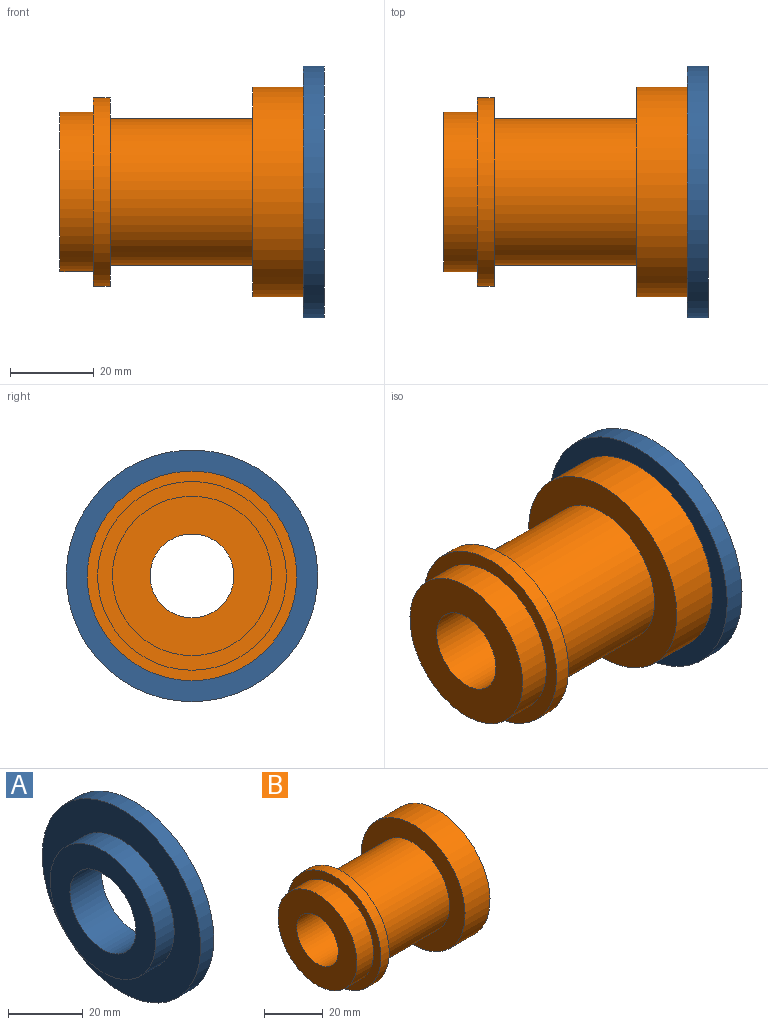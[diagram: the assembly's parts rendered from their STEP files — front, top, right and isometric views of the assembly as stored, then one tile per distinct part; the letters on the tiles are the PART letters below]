
ASSEMBLY  parts=2 mates=1
PART A: 6 faces, bbox 12x60x60 mm
  f0: cylinder r=12.5mm len=25mm, axis (1,0,0), area 942.5mm2, adj f1,f5
  f1: plane 60x60mm, normal (1,0,0), area 2336.6mm2, adj f0,f2
  f2: cylinder r=30mm len=60mm, axis (1,0,0), area 942.5mm2, adj f1,f3
  f3: plane 60x60mm, normal (-1,0,0), area 1570.8mm2, adj f2,f4
  f4: cylinder r=20mm len=40mm, axis (1,0,0), area 879.6mm2, adj f3,f5
  f5: plane 40x40mm, normal (-1,0,0), area 765.8mm2, adj f0,f4
PART B: 12 faces, bbox 58x50x50 mm
  f0: plane 50x50mm, normal (1,0,0), area 706.9mm2, adj f1,f11
  f1: cylinder r=25mm len=50mm, axis (1,0,0), area 1885mm2, adj f0,f2
  f2: plane 50x50mm, normal (-1,0,0), area 1001.4mm2, adj f1,f3
  f3: cylinder r=17.5mm len=35mm, axis (1,0,0), area 3738.5mm2, adj f2,f4
  f4: plane 45x45mm, normal (1,0,0), area 628.3mm2, adj f3,f5
  f5: cylinder r=22.5mm len=45mm, axis (1,0,0), area 565.5mm2, adj f4,f6
  f6: plane 45x45mm, normal (-1,0,0), area 456.3mm2, adj f5,f7
  f7: cylinder r=19mm len=38mm, axis (1,0,0), area 955mm2, adj f6,f8
  f8: plane 38x38mm, normal (-1,0,0), area 820mm2, adj f7,f9
  f9: cylinder r=10mm len=51mm, axis (1,0,0), area 3204.4mm2, adj f8,f10
  f10: plane 40x40mm, normal (1,0,0), area 942.5mm2, adj f9,f11
  f11: cylinder r=20mm len=40mm, axis (1,0,0), area 879.6mm2, adj f0,f10
PLACE A at identity
PLACE B t=(-5,0,0)mm
MATE cylindrical B.f1 <-> A.f0  axis (1,0,0) through (-12,0,0)mm
